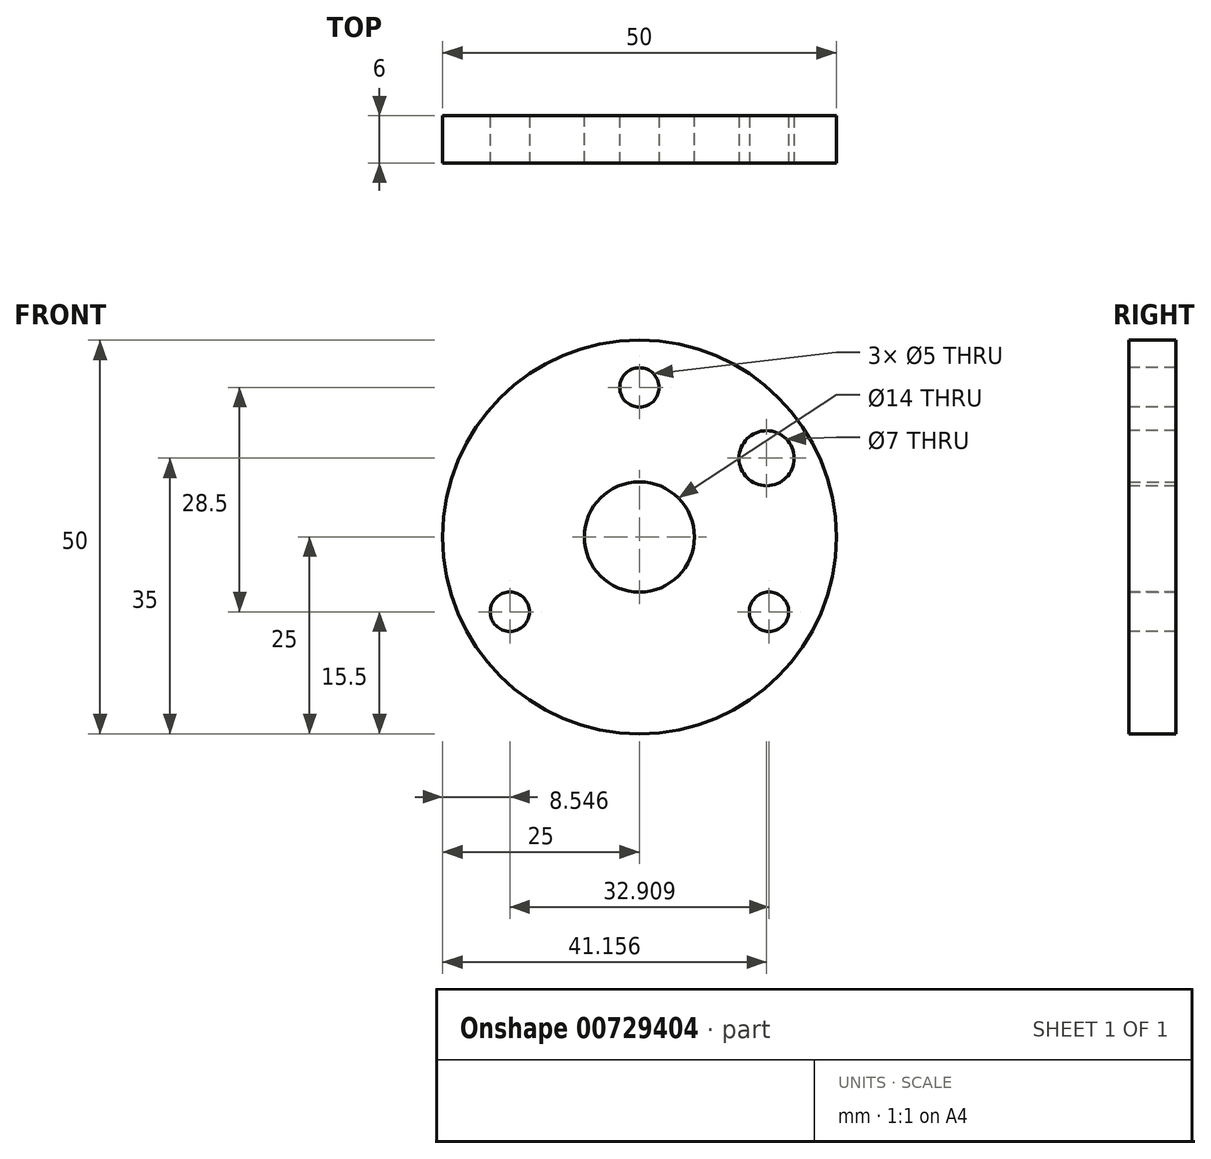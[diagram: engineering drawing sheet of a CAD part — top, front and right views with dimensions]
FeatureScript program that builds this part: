
annotation { "Feature Type Name" : "Feature", "Feature Type Description" : "" }
export const myFeature = defineFeature(function(context is Context, id is Id, definition is map)
    precondition{}
    {
        {
            var Q0;
            Q0=qCreatedBy(makeId("Front.planeOp"),FACE);
            var sketch = newSketch(context, id + "F0", { "sketchPlane" : qUnion([Q0])});
            skCircle(sketch, "E0", {"center": v(0, 0) * mm, "radius": 25 * mm});
            skCircle(sketch, "E1", {"center": v(0, 0) * mm, "radius": 7 * mm});
            skSolve(sketch);
        }
        {
            var Q0;
            Q0 = qSketchRegion(id + "F0", true);
            extrude(context, id + "F1", {"entities" : qUnion([Q0]), "depth" : 6 * mm, "offsetDistance" : 25 * mm});
        }
        {
            var Q0;
            Q0=makeQuery(id+"F1.opExtrude","CAP_FACE",FACE,{"disambiguationData":[OSD([sQuery(id+"F0.wireOp",EDGE,"E0"),sQuery(id+"F0.wireOp",EDGE,"E1")])],"isStart":false});
            var sketch = newSketch(context, id + "F2", { "sketchPlane" : qUnion([Q0])});
            skCircle(sketch, "E2", {"center": v(0, 19) * mm, "radius": 2.5 * mm});
            skCircle(sketch, "E3.1.0", {"center": v(-16.45, -9.5) * mm, "radius": 2.5 * mm});
            skCircle(sketch, "E3.2.0", {"center": v(16.45, -9.5) * mm, "radius": 2.5 * mm});
            skPoint(sketch, "E3.center", {"position": v(0, 0) * mm});
            skSolve(sketch);
        }
        {
            var Q0;
            Q0=sQuery(id+"F2.wireOp",VERTEX,"E2.center");
            var Q1;
            Q1=sQuery(id+"F2.wireOp",VERTEX,"E3.2.0.center");
            var Q2;
            Q2=sQuery(id+"F2.wireOp",VERTEX,"E3.1.0.center");
            var Q3;
            Q3=makeQuery(id+"F1.opExtrude","SWEPT_BODY",BODY,{"disambiguationData":[OSD([sQuery(id+"F0.wireOp",EDGE,"E0"),sQuery(id+"F0.wireOp",EDGE,"E1")])]});
            hole(context, id + "F3", {"style" : HoleStyle.SIMPLE, "endStyle" : HoleEndStyle.THROUGH, "holeDiameter" : 5 * mm, "majorDiameter" : 5 * mm, "isTappedThrough" : true, "tappedDepth" : 12 * mm, "tapClearance" : 3, "locations" : qUnion([Q0, Q1, Q2]), "scope" : qUnion([Q3])});
        }
        {
            var Q0;
            Q0=makeQuery(id+"F2.imprint","IMPRINT",FACE,{"disambiguationData":[TD([[makeQuery(id+"F2.imprint","IMPRINT",EDGE,{"derivedFrom":sQuery(id+"F2.wireOp",EDGE,"E2")}),-1.0]])]});
            var sketch = newSketch(context, id + "F4", { "sketchPlane" : qUnion([Q0])});
            skCircle(sketch, "E4", {"center": v(16.16, 10) * mm, "radius": 3.5 * mm});
            skSolve(sketch);
        }
        {
            var Q0;
            Q0 = qSketchRegion(id + "F4", true);
            extrude(context, id + "F5", {"entities" : qUnion([Q0]), "operationType" : NewBodyOperationType.REMOVE, "endBound" : BoundingType.UP_TO_NEXT, "oppositeDirection" : true, "depth" : 25 * mm, "offsetDistance" : 25 * mm});
        }
        {
            var Q0;
            Q0=qCreatedBy(makeId("Top.planeOp"),FACE);
            var sketch = newSketch(context, id + "F6", { "sketchPlane" : qUnion([Q0])});
            skLineSegment(sketch, "E5", {"start": v(0, 0) * mm, "end": v(0, 35.27) * mm, "construction": true});
            skSolve(sketch);
        }
    });
